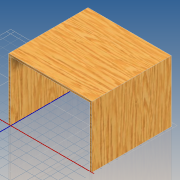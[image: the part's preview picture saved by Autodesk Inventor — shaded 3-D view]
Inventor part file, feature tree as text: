
AUTODESK INVENTOR PART (.ipt)
format: ipt  version: 2020 (Build 240168000, 168)  size: 142,336 bytes
history: native  units: mm
features: extrude x2, sketch x1
ambient origin geometry x8: Origin, YZ Plane, XZ Plane, XY Plane, X Axis, Y Axis, Z Axis, Center Point
bodies: Solid1 (feature_tree)
feature tree (3):
  sketch  "Sketch1"  dims[d0=400.0mm d1=300.0mm d2=400.0mm d3=0.0mm d4=10.0mm d7=400.0mm d8=0.0mm]
  extrude  "Extrusion1"  Depth=300.0mm
  extrude  "Extrusion2"  Depth=400.0mm TaperAngle=0.0deg
